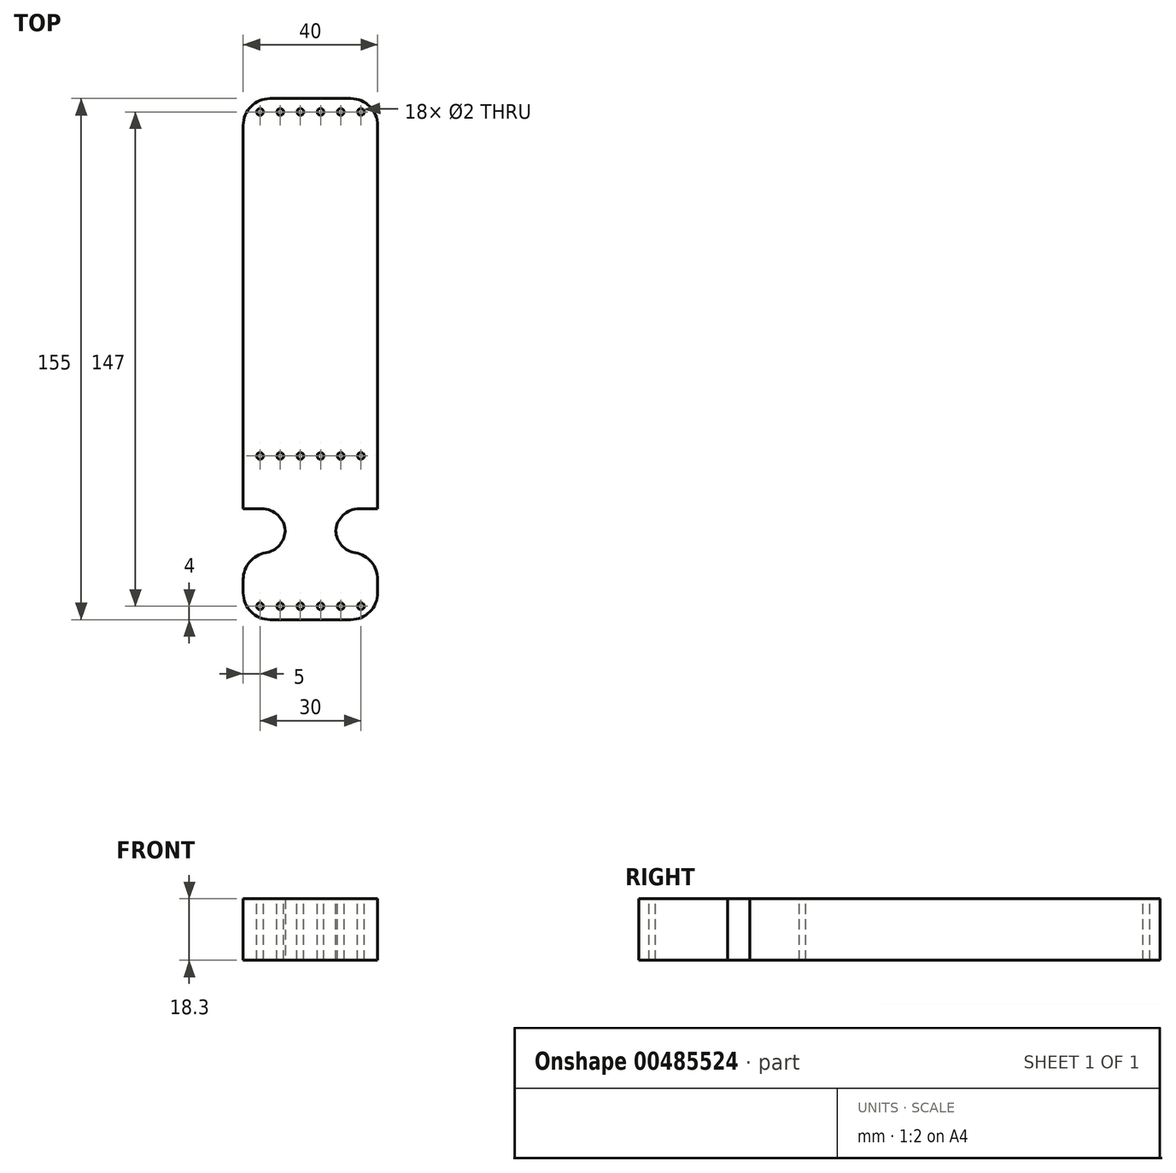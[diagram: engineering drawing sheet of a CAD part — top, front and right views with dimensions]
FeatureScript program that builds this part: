
annotation { "Feature Type Name" : "Feature", "Feature Type Description" : "" }
export const myFeature = defineFeature(function(context is Context, id is Id, definition is map)
    precondition{}
    {
        {
            var Q0;
            Q0=qCreatedBy(makeId("Top.planeOp"),FACE);
            var sketch = newSketch(context, id + "F0", { "sketchPlane" : qUnion([Q0])});
            skLineSegment(sketch, "E0.bottom", {"start": v(-20, 77.5) * mm, "end": v(20, 77.5) * mm});
            skLineSegment(sketch, "E0.top", {"start": v(-20, -77.5) * mm, "end": v(20, -77.5) * mm});
            skLineSegment(sketch, "E0.left", {"start": v(-20, 77.5) * mm, "end": v(-20, -77.5) * mm});
            skLineSegment(sketch, "E0.right", {"start": v(20, 77.5) * mm, "end": v(20, -77.5) * mm});
            skSolve(sketch);
        }
        {
            var Q0;
            Q0=qSketchRegion(id+"F0",true);
            extrude(context, id + "F1", {"entities" : qUnion([Q0]), "depth" : 3 * mm});
        }
        {
            var Q0;
            Q0=makeQuery(id+"F1.opExtrude","CAP_FACE",FACE,{"disambiguationData":[OSD([sQuery(id+"F0.wireOp",EDGE,"E0.bottom"),sQuery(id+"F0.wireOp",EDGE,"E0.top"),sQuery(id+"F0.wireOp",EDGE,"E0.left"),sQuery(id+"F0.wireOp",EDGE,"E0.right")])],"isStart":false});
            var sketch = newSketch(context, id + "F2", { "sketchPlane" : qUnion([Q0])});
            skLineSegment(sketch, "E1.bottom", {"start": v(-20, -57.5) * mm, "end": v(20, -57.5) * mm});
            skLineSegment(sketch, "E1.top", {"start": v(-20, -44.5) * mm, "end": v(20, -44.5) * mm});
            skLineSegment(sketch, "E1.left", {"start": v(-20, -57.5) * mm, "end": v(-20, -44.5) * mm});
            skLineSegment(sketch, "E1.right", {"start": v(20, -57.5) * mm, "end": v(20, -44.5) * mm});
            skLineSegment(sketch, "E2.bottom", {"start": v(-7.5, -44.5) * mm, "end": v(7.5, -44.5) * mm});
            skLineSegment(sketch, "E2.top", {"start": v(-7.5, -57.5) * mm, "end": v(7.5, -57.5) * mm});
            skLineSegment(sketch, "E2.left", {"start": v(-7.5, -44.5) * mm, "end": v(-7.5, -57.5) * mm});
            skLineSegment(sketch, "E2.right", {"start": v(7.5, -44.5) * mm, "end": v(7.5, -57.5) * mm});
            skSolve(sketch);
        }
        {
            var Q0;
            {var subQ0=sQuery(id+"F2.wireOp",EDGE,"E1.left");Q0=makeQuery(id+"F2.imprint","IMPRINT",FACE,{"disambiguationData":[TD([[makeQuery(id+"F2.imprint","IMPRINT",EDGE,{"derivedFrom":subQ0}),1.0]])]});}
            var Q1;
            {var subQ0=sQuery(id+"F2.wireOp",EDGE,"E1.right");Q1=makeQuery(id+"F2.imprint","IMPRINT",FACE,{"disambiguationData":[TD([[makeQuery(id+"F2.imprint","IMPRINT",EDGE,{"derivedFrom":subQ0}),-1.0]])]});}
            extrude(context, id + "F3", {"entities" : qUnion([Q0, Q1]), "operationType" : NewBodyOperationType.REMOVE, "endBound" : BoundingType.UP_TO_NEXT, "oppositeDirection" : true, "depth" : 25 * mm});
        }
        {
            var Q0;
            Q0=makeQuery(id+"F3.boolean.opBoolean","COPY",EDGE,{"derivedFrom":makeQuery(id+"F3.opExtrude","SWEPT_EDGE",EDGE,{"disambiguationData":[OSD([sQuery(id+"F0.wireOp",EDGE,"E0.left"),sQuery(id+"F2.wireOp",EDGE,"E1.top"),sQuery(id+"F2.wireOp",EDGE,"E1.left")])]})});
            var Q1;
            Q1=makeQuery(id+"F3.boolean.opBoolean","COPY",EDGE,{"derivedFrom":makeQuery(id+"F3.opExtrude","SWEPT_EDGE",EDGE,{"disambiguationData":[OSD([sQuery(id+"F0.wireOp",EDGE,"E0.right"),sQuery(id+"F2.wireOp",EDGE,"E1.top"),sQuery(id+"F2.wireOp",EDGE,"E1.right")])]})});
            var Q2;
            Q2=makeQuery(id+"F3.boolean.opBoolean","COPY",EDGE,{"derivedFrom":makeQuery(id+"F3.opExtrude","SWEPT_EDGE",EDGE,{"disambiguationData":[OSD([sQuery(id+"F0.wireOp",EDGE,"E0.right"),sQuery(id+"F2.wireOp",EDGE,"E1.bottom"),sQuery(id+"F2.wireOp",EDGE,"E1.right")])]})});
            var Q3;
            Q3=makeQuery(id+"F3.boolean.opBoolean","COPY",EDGE,{"derivedFrom":makeQuery(id+"F3.opExtrude","SWEPT_EDGE",EDGE,{"disambiguationData":[OSD([sQuery(id+"F0.wireOp",EDGE,"E0.left"),sQuery(id+"F2.wireOp",EDGE,"E1.bottom"),sQuery(id+"F2.wireOp",EDGE,"E1.left")])]})});
            var Q4;
            Q4=makeQuery(id+"F1.opExtrude","SWEPT_EDGE",EDGE,{"disambiguationData":[OSD([sQuery(id+"F0.wireOp",EDGE,"E0.top"),sQuery(id+"F0.wireOp",EDGE,"E0.left")])]});
            var Q5;
            Q5=makeQuery(id+"F1.opExtrude","SWEPT_EDGE",EDGE,{"disambiguationData":[OSD([sQuery(id+"F0.wireOp",EDGE,"E0.top"),sQuery(id+"F0.wireOp",EDGE,"E0.right")])]});
            var Q6;
            Q6=makeQuery(id+"F1.opExtrude","SWEPT_EDGE",EDGE,{"disambiguationData":[OSD([sQuery(id+"F0.wireOp",EDGE,"E0.bottom"),sQuery(id+"F0.wireOp",EDGE,"E0.left")])]});
            var Q7;
            Q7=makeQuery(id+"F1.opExtrude","SWEPT_EDGE",EDGE,{"disambiguationData":[OSD([sQuery(id+"F0.wireOp",EDGE,"E0.bottom"),sQuery(id+"F0.wireOp",EDGE,"E0.right")])]});
            fillet(context, id + "F4", {"entities" : qUnion([Q0, Q1, Q2, Q3, Q4, Q5, Q6, Q7]), "radius" : 8 * mm, "tangentPropagation" : true, "allowEdgeOverflow" : false});
        }
        {
            var Q0;
            Q0=makeQuery(id+"F3.boolean.opBoolean","COPY",EDGE,{"derivedFrom":makeQuery(id+"F3.opExtrude","SWEPT_EDGE",EDGE,{"disambiguationData":[OSD([sQuery(id+"F2.wireOp",EDGE,"E1.top"),sQuery(id+"F2.wireOp",EDGE,"E2.bottom"),sQuery(id+"F2.wireOp",EDGE,"E2.left")])]})});
            var Q1;
            Q1=makeQuery(id+"F3.boolean.opBoolean","COPY",EDGE,{"derivedFrom":makeQuery(id+"F3.opExtrude","SWEPT_EDGE",EDGE,{"disambiguationData":[OSD([sQuery(id+"F2.wireOp",EDGE,"E1.bottom"),sQuery(id+"F2.wireOp",EDGE,"E2.top"),sQuery(id+"F2.wireOp",EDGE,"E2.left")])]})});
            var Q2;
            Q2=makeQuery(id+"F3.boolean.opBoolean","COPY",EDGE,{"derivedFrom":makeQuery(id+"F3.opExtrude","SWEPT_EDGE",EDGE,{"disambiguationData":[OSD([sQuery(id+"F2.wireOp",EDGE,"E1.top"),sQuery(id+"F2.wireOp",EDGE,"E2.bottom"),sQuery(id+"F2.wireOp",EDGE,"E2.right")])]})});
            var Q3;
            Q3=makeQuery(id+"F3.boolean.opBoolean","COPY",EDGE,{"derivedFrom":makeQuery(id+"F3.opExtrude","SWEPT_EDGE",EDGE,{"disambiguationData":[OSD([sQuery(id+"F2.wireOp",EDGE,"E1.bottom"),sQuery(id+"F2.wireOp",EDGE,"E2.top"),sQuery(id+"F2.wireOp",EDGE,"E2.right")])]})});
            fillet(context, id + "F5", {"entities" : qUnion([Q0, Q1, Q2, Q3]), "radius" : 7 * mm, "tangentPropagation" : true, "allowEdgeOverflow" : false});
        }
        {
            var Q0;
            Q0=makeQuery(id+"F1.opExtrude","CAP_FACE",FACE,{"disambiguationData":[OSD([sQuery(id+"F0.wireOp",EDGE,"E0.bottom"),sQuery(id+"F0.wireOp",EDGE,"E0.top"),sQuery(id+"F0.wireOp",EDGE,"E0.left"),sQuery(id+"F0.wireOp",EDGE,"E0.right")])],"isStart":false});
            var sketch = newSketch(context, id + "F6", { "sketchPlane" : qUnion([Q0])});
            skCircle(sketch, "E3", {"center": v(-15, -73.5) * mm, "radius": 1 * mm});
            skCircle(sketch, "E4.1.0.0", {"center": v(-9, -73.5) * mm, "radius": 1 * mm});
            skCircle(sketch, "E4.2.0.0", {"center": v(-3, -73.5) * mm, "radius": 1 * mm});
            skCircle(sketch, "E4.3.0.0", {"center": v(3, -73.5) * mm, "radius": 1 * mm});
            skLineSegment(sketch, "E4.direction1", {"start": v(-15, -73.5) * mm, "end": v(-9, -73.5) * mm, "construction": true});
            skCircle(sketch, "E5", {"center": v(-15, -28.8) * mm, "radius": 1 * mm});
            skCircle(sketch, "E6.1.0.0", {"center": v(-9, -28.8) * mm, "radius": 1 * mm});
            skCircle(sketch, "E6.2.0.0", {"center": v(-3, -28.8) * mm, "radius": 1 * mm});
            skCircle(sketch, "E6.3.0.0", {"center": v(3, -28.8) * mm, "radius": 1 * mm});
            skLineSegment(sketch, "E6.direction1", {"start": v(-15, -28.8) * mm, "end": v(-9, -28.8) * mm, "construction": true});
            skCircle(sketch, "E7", {"center": v(-15, 73.5) * mm, "radius": 1 * mm});
            skCircle(sketch, "E8.1.0.0", {"center": v(-9, 73.5) * mm, "radius": 1 * mm});
            skCircle(sketch, "E8.2.0.0", {"center": v(-3, 73.5) * mm, "radius": 1 * mm});
            skCircle(sketch, "E8.3.0.0", {"center": v(3, 73.5) * mm, "radius": 1 * mm});
            skLineSegment(sketch, "E8.direction1", {"start": v(-15, 73.5) * mm, "end": v(-9, 73.5) * mm, "construction": true});
            skCircle(sketch, "E9.0.4.0", {"center": v(9, -73.5) * mm, "radius": 1 * mm});
            skCircle(sketch, "E9.0.5.0", {"center": v(15, -73.5) * mm, "radius": 1 * mm});
            skCircle(sketch, "E10.0.4.0", {"center": v(9, -28.8) * mm, "radius": 1 * mm});
            skCircle(sketch, "E10.0.5.0", {"center": v(15, -28.8) * mm, "radius": 1 * mm});
            skCircle(sketch, "E11.0.4.0", {"center": v(9, 73.5) * mm, "radius": 1 * mm});
            skCircle(sketch, "E11.0.5.0", {"center": v(15, 73.5) * mm, "radius": 1 * mm});
            skSolve(sketch);
        }
        {
            var Q0;
            Q0=qSketchRegion(id+"F6",true);
            extrude(context, id + "F7", {"entities" : qUnion([Q0]), "operationType" : NewBodyOperationType.REMOVE, "endBound" : BoundingType.UP_TO_NEXT, "oppositeDirection" : true, "depth" : 25 * mm});
        }
        {
            var Q0;
            Q0=makeQuery(id+"F1.opExtrude","CAP_FACE",FACE,{"disambiguationData":[OSD([sQuery(id+"F0.wireOp",EDGE,"E0.bottom"),sQuery(id+"F0.wireOp",EDGE,"E0.top"),sQuery(id+"F0.wireOp",EDGE,"E0.left"),sQuery(id+"F0.wireOp",EDGE,"E0.right")])],"isStart":false});
            extrude(context, id + "F8", {"entities" : qUnion([Q0]), "operationType" : NewBodyOperationType.ADD, "depth" : 15.3 * mm});
        }
    });
